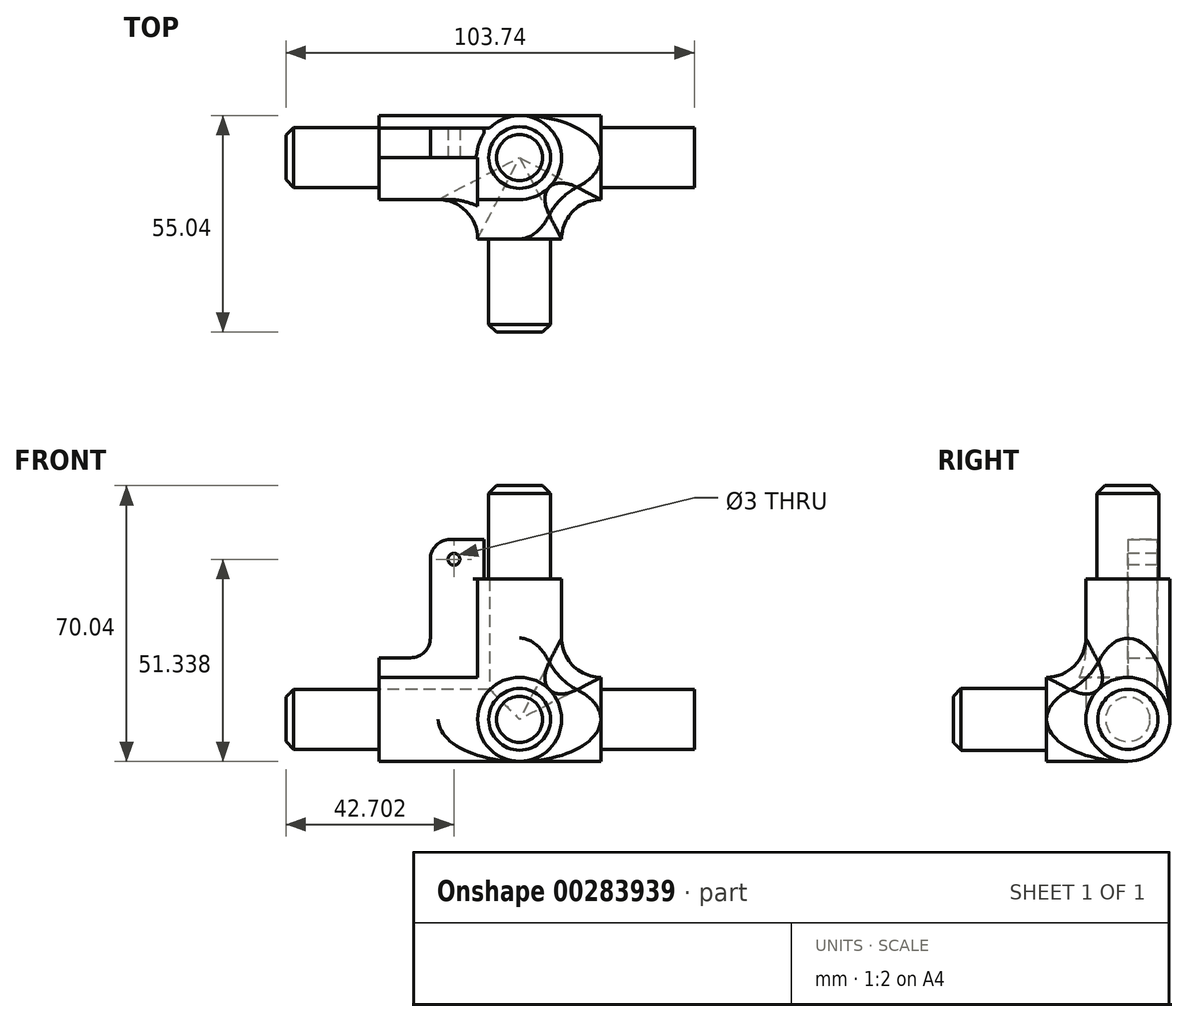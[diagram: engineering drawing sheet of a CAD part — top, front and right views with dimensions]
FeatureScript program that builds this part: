
annotation { "Feature Type Name" : "Feature", "Feature Type Description" : "" }
export const myFeature = defineFeature(function(context is Context, id is Id, definition is map)
    precondition{}
    {
        {
            var Q0;
            Q0=qCreatedBy(makeId("Right.planeOp"),FACE);
            var sketch = newSketch(context, id + "F0", { "sketchPlane" : qUnion([Q0])});
            skCircle(sketch, "E0", {"center": v(0, 0) * mm, "radius": 10.67 * mm});
            skSolve(sketch);
        }
        {
            var Q0;
            Q0=qSketchRegion(id+"F0",true);
            extrude(context, id + "F1", {"entities" : qUnion([Q0]), "endBound" : BoundingType.SYMMETRIC, "depth" : 21.34 * mm + 20 * mm});
        }
        {
            var Q0;
            Q0=makeQuery(id+"F1.opExtrude","CAP_FACE",FACE,{"disambiguationData":[OSD([sQuery(id+"F0.wireOp",EDGE,"E0")])],"isStart":false});
            var sketch = newSketch(context, id + "F2", { "sketchPlane" : qUnion([Q0])});
            skCircle(sketch, "E1", {"center": v(0, 0) * mm, "radius": 7.9 * mm});
            skSolve(sketch);
        }
        {
            var Q0;
            Q0=qSketchRegion(id+"F2",true);
            extrude(context, id + "F3", {"entities" : qUnion([Q0]), "operationType" : NewBodyOperationType.ADD, "depth" : 15.8 * mm * 1.5});
        }
        {
            var Q0;
            Q0=makeQuery(id+"F3.opExtrude","CAP_FACE",FACE,{"disambiguationData":[OSD([sQuery(id+"F2.wireOp",EDGE,"E1")])],"isStart":false});
            var sketch = newSketch(context, id + "F4", { "sketchPlane" : qUnion([Q0])});
            skCircle(sketch, "E2.0", {"center": v(0, 0) * mm, "radius": 7.9 * mm});
            skCircle(sketch, "E3", {"center": v(0, 0) * mm, "radius": 7.65 * mm});
            skSolve(sketch);
        }
        {
            var Q0;
            Q0=qSketchRegion(id+"F4",true);
            var Q1;
            Q1=makeQuery(id+"F1.opExtrude","CAP_FACE",FACE,{"disambiguationData":[OSD([sQuery(id+"F0.wireOp",EDGE,"E0")])],"isStart":false});
            extrude(context, id + "F5", {"entities" : qUnion([Q0]), "operationType" : NewBodyOperationType.REMOVE, "endBound" : BoundingType.UP_TO_SURFACE, "oppositeDirection" : true, "endBoundEntityFace" : qUnion([Q1]), "depth" : 25 * mm});
        }
        {
            var Q0;
            Q0=makeQuery(id+"F1.opExtrude","CAP_FACE",FACE,{"disambiguationData":[OSD([sQuery(id+"F0.wireOp",EDGE,"E0")])],"isStart":true});
            var sketch = newSketch(context, id + "F6", { "sketchPlane" : qUnion([Q0])});
            skCircle(sketch, "E4", {"center": v(0, 0) * mm, "radius": 7.65 * mm});
            skSolve(sketch);
        }
        {
            var Q0;
            Q0=qSketchRegion(id+"F6",true);
            extrude(context, id + "F7", {"entities" : qUnion([Q0]), "operationType" : NewBodyOperationType.ADD, "depth" : 15.8 * mm * 1.5 + 15 * mm});
        }
        {
            var Q0;
            Q0=qCreatedBy(makeId("Top.planeOp"),FACE);
            var sketch = newSketch(context, id + "F8", { "sketchPlane" : qUnion([Q0])});
            skCircle(sketch, "E5", {"center": v(0, 0) * mm, "radius": 10.67 * mm});
            skSolve(sketch);
        }
        {
            var Q0;
            Q0=qSketchRegion(id+"F8",true);
            extrude(context, id + "F9", {"entities" : qUnion([Q0]), "operationType" : NewBodyOperationType.ADD, "depth" : 21.34 * mm / 2 + 25 * mm});
        }
        {
            var Q0;
            Q0=makeQuery(id+"F9.opExtrude","CAP_FACE",FACE,{"disambiguationData":[OSD([sQuery(id+"F8.wireOp",EDGE,"E5")])],"isStart":false});
            var sketch = newSketch(context, id + "F10", { "sketchPlane" : qUnion([Q0])});
            skCircle(sketch, "E6", {"center": v(0, 0) * mm, "radius": 7.84 * mm});
            skSolve(sketch);
        }
        {
            var Q0;
            Q0=qSketchRegion(id+"F10",true);
            extrude(context, id + "F11", {"entities" : qUnion([Q0]), "operationType" : NewBodyOperationType.ADD, "depth" : 15.8 * mm * 1.5});
        }
        {
            var Q0;
            Q0=qCreatedBy(makeId("Front.planeOp"),FACE);
            var sketch = newSketch(context, id + "F12", { "sketchPlane" : qUnion([Q0])});
            skCircle(sketch, "E7", {"center": v(0, 0) * mm, "radius": 10.67 * mm});
            skSolve(sketch);
        }
        {
            var Q0;
            Q0=qSketchRegion(id+"F12",true);
            extrude(context, id + "F13", {"entities" : qUnion([Q0]), "operationType" : NewBodyOperationType.ADD, "depth" : 21.34 * mm / 2 + 10 * mm});
        }
        {
            var Q0;
            Q0=makeQuery(id+"F13.opExtrude","CAP_FACE",FACE,{"disambiguationData":[OSD([sQuery(id+"F12.wireOp",EDGE,"E7")])],"isStart":false});
            var sketch = newSketch(context, id + "F14", { "sketchPlane" : qUnion([Q0])});
            skCircle(sketch, "E8", {"center": v(0, 0) * mm, "radius": 7.84 * mm});
            skSolve(sketch);
        }
        {
            var Q0;
            Q0=qSketchRegion(id+"F14",true);
            extrude(context, id + "F15", {"entities" : qUnion([Q0]), "operationType" : NewBodyOperationType.ADD, "depth" : 15.8 * mm * 1.5});
        }
        {
            var Q0;
            Q0=makeQuery(id+"F11.opExtrude","CAP_EDGE",EDGE,{"disambiguationData":[OSD([sQuery(id+"F10.wireOp",EDGE,"E6")])],"isStart":false});
            var Q1;
            Q1=makeQuery(id+"F5.boolean.opBoolean","COPY",EDGE,{"derivedFrom":makeQuery(id+"F5.opExtrude","CAP_EDGE",EDGE,{"disambiguationData":[OSD([sQuery(id+"F4.wireOp",EDGE,"E3")])],"isStart":true})});
            var Q2;
            Q2=makeQuery(id+"F7.opExtrude","CAP_EDGE",EDGE,{"disambiguationData":[OSD([sQuery(id+"F6.wireOp",EDGE,"E4")])],"isStart":false});
            var Q3;
            Q3=makeQuery(id+"F15.opExtrude","CAP_EDGE",EDGE,{"disambiguationData":[OSD([sQuery(id+"F14.wireOp",EDGE,"E8")])],"isStart":false});
            chamfer(context, id + "F16", {"entities" : qUnion([Q0, Q1, Q2, Q3]), "width" : 2 * mm, "tangentPropagation" : true});
        }
        {
            var Q0;
            Q0=makeQuery(id+"F1.opExtrude","CAP_FACE",FACE,{"disambiguationData":[OSD([sQuery(id+"F0.wireOp",EDGE,"E0")])],"isStart":true});
            extrude(context, id + "F17", {"entities" : qUnion([Q0]), "operationType" : NewBodyOperationType.ADD, "depth" : 15 * mm});
        }
        {
            var Q0;
            Q0=qCreatedBy(makeId("Front.planeOp"),FACE);
            var sketch = newSketch(context, id + "F18", { "sketchPlane" : qUnion([Q0])});
            skLineSegment(sketch, "E9.0", {"start": v(-35.67, 10.67) * mm, "end": v(-35.67, -10.67) * mm, "construction": true});
            skLineSegment(sketch, "E9.1", {"start": v(-10.67, 35.67) * mm, "end": v(10.67, 35.67) * mm, "construction": true});
            skLineSegment(sketch, "E10.bottom", {"start": v(0, 0) * mm, "end": v(-35.67, 0) * mm});
            skLineSegment(sketch, "E10.top", {"start": v(0, 35.67) * mm, "end": v(-35.67, 35.67) * mm});
            skLineSegment(sketch, "E10.left", {"start": v(0, 0) * mm, "end": v(0, 35.67) * mm});
            skLineSegment(sketch, "E10.right", {"start": v(-35.67, 0) * mm, "end": v(-35.67, 35.67) * mm});
            skSolve(sketch);
        }
        {
            var Q0;
            Q0 = qSketchRegion(id + "F18", true);
            extrude(context, id + "F19", {"entities" : qUnion([Q0]), "operationType" : NewBodyOperationType.ADD, "oppositeDirection" : true, "depth" : 7.5 * mm});
        }
        {
            var Q0;
            Q0=makeQuery(id+"F19.opExtrude","SWEPT_EDGE",EDGE,{"disambiguationData":[OSD([sQuery(id+"F18.wireOp",EDGE,"E10.top"),sQuery(id+"F18.wireOp",EDGE,"E10.right")])]});
            fillet(context, id + "F20", {"entities" : qUnion([Q0]), "radius" : 5 * mm, "tangentPropagation" : true, "allowEdgeOverflow" : false});
        }
        {
            var Q0;
            Q0=makeQuery(id+"F19.boolean.opBoolean","MERGE",FACE,{"derivedFrom":[makeQuery(id+"F9.opExtrude","CAP_FACE",FACE,{"disambiguationData":[OSD([sQuery(id+"F8.wireOp",EDGE,"E5")])],"isStart":false}),makeQuery(id+"F19.opExtrude","SWEPT_FACE",FACE,{"disambiguationData":[OSD([sQuery(id+"F18.wireOp",EDGE,"E10.top")])]})]});
            var sketch = newSketch(context, id + "F21", { "sketchPlane" : qUnion([Q0])});
            skArc(sketch, "E11.0", {"start": v(-10.67, 0) * mm, "mid": v(-7.54, -7.54) * mm, "end": v(0, -10.67) * mm});
            skLineSegment(sketch, "E12", {"start": v(-10.67, 0) * mm, "end": v(-10.67, -10.67) * mm});
            skLineSegment(sketch, "E13", {"start": v(-10.67, -10.67) * mm, "end": v(0, -10.67) * mm});
            skLineSegment(sketch, "E14", {"start": v(0, -10.67) * mm, "end": v(0, 0) * mm, "construction": true});
            skPoint(sketch, "E15.orphan", {"position": v(-7.59, 7.5) * mm});
            skSolve(sketch);
        }
        {
            var Q0;
            Q0 = qSketchRegion(id + "F21", true);
            extrude(context, id + "F22", {"entities" : qUnion([Q0]), "operationType" : NewBodyOperationType.ADD, "endBound" : BoundingType.UP_TO_NEXT, "oppositeDirection" : true, "depth" : 25 * mm});
        }
        {
            var Q0;
            Q0=makeQuery(id+"F19.boolean.opBoolean","MERGE",FACE,{"derivedFrom":[makeQuery(id+"F17.opExtrude","CAP_FACE",FACE,{"disambiguationData":[OSD([sQuery(id+"F0.wireOp",EDGE,"E0")])],"isStart":false}),makeQuery(id+"F19.opExtrude","SWEPT_FACE",FACE,{"disambiguationData":[OSD([sQuery(id+"F18.wireOp",EDGE,"E10.right")])]})]});
            var sketch = newSketch(context, id + "F23", { "sketchPlane" : qUnion([Q0])});
            skArc(sketch, "E16.0", {"start": v(0, 10.67) * mm, "mid": v(7.54, 7.54) * mm, "end": v(10.67, 0) * mm});
            skLineSegment(sketch, "E17", {"start": v(0, 10.67) * mm, "end": v(10.67, 10.67) * mm});
            skLineSegment(sketch, "E18", {"start": v(10.67, 10.67) * mm, "end": v(10.67, 0) * mm});
            skLineSegment(sketch, "E19", {"start": v(10.67, 0) * mm, "end": v(0, 0) * mm, "construction": true});
            skPoint(sketch, "E20.orphan", {"position": v(-7.5, 7.59) * mm});
            skSolve(sketch);
        }
        {
            var Q0;
            Q0 = qSketchRegion(id + "F23", true);
            var Q1;
            Q1=makeQuery(id+"F22.opExtrude","SWEPT_FACE",FACE,{"disambiguationData":[OSD([sQuery(id+"F21.wireOp",EDGE,"E12")])]});
            extrude(context, id + "F24", {"entities" : qUnion([Q0]), "operationType" : NewBodyOperationType.ADD, "endBound" : BoundingType.UP_TO_SURFACE, "oppositeDirection" : true, "endBoundEntityFace" : qUnion([Q1]), "depth" : 25 * mm});
        }
        {
            var Q0;
            Q0=makeQuery(id+"F13.boolean.opBoolean","INTERSECT",EDGE,{"disambiguationData":[OD(0.0)],"derivedFrom":[makeQuery(id+"F1.opExtrude","SWEPT_FACE",FACE,{"disambiguationData":[OSD([sQuery(id+"F0.wireOp",EDGE,"E0")])]}),makeQuery(id+"F13.opExtrude","SWEPT_FACE",FACE,{"disambiguationData":[OSD([sQuery(id+"F12.wireOp",EDGE,"E7")])]})]});
            var Q1;
            Q1=makeQuery(id+"F13.boolean.opBoolean","INTERSECT",EDGE,{"disambiguationData":[OD(1.0)],"derivedFrom":[makeQuery(id+"F1.opExtrude","SWEPT_FACE",FACE,{"disambiguationData":[OSD([sQuery(id+"F0.wireOp",EDGE,"E0")])]}),makeQuery(id+"F13.opExtrude","SWEPT_FACE",FACE,{"disambiguationData":[OSD([sQuery(id+"F12.wireOp",EDGE,"E7")])]})]});
            var Q2;
            Q2=makeQuery(id+"F9.boolean.opBoolean","INTERSECT",EDGE,{"disambiguationData":[OD(1.0)],"derivedFrom":[makeQuery(id+"F1.opExtrude","SWEPT_FACE",FACE,{"disambiguationData":[OSD([sQuery(id+"F0.wireOp",EDGE,"E0")])]}),makeQuery(id+"F9.opExtrude","SWEPT_FACE",FACE,{"disambiguationData":[OSD([sQuery(id+"F8.wireOp",EDGE,"E5")])]})]});
            var Q3;
            Q3=makeQuery(id+"F13.boolean.opBoolean","INTERSECT",EDGE,{"derivedFrom":[makeQuery(id+"F9.opExtrude","SWEPT_FACE",FACE,{"disambiguationData":[OSD([sQuery(id+"F8.wireOp",EDGE,"E5")])]}),makeQuery(id+"F13.opExtrude","SWEPT_FACE",FACE,{"disambiguationData":[OSD([sQuery(id+"F12.wireOp",EDGE,"E7")])]})]});
            fillet(context, id + "F25", {"entities" : qUnion([Q0, Q1, Q2, Q3]), "radius" : 10 * mm, "tangentPropagation" : true, "allowEdgeOverflow" : false});
        }
        {
            var Q0;
            Q0=makeQuery(id+"F22.boolean.opBoolean","MERGE",FACE,{"derivedFrom":[makeQuery(id+"F19.boolean.opBoolean","MERGE",FACE,{"derivedFrom":[makeQuery(id+"F9.opExtrude","CAP_FACE",FACE,{"disambiguationData":[OSD([sQuery(id+"F8.wireOp",EDGE,"E5")])],"isStart":false}),makeQuery(id+"F19.opExtrude","SWEPT_FACE",FACE,{"disambiguationData":[OSD([sQuery(id+"F18.wireOp",EDGE,"E10.top")])]})]}),makeQuery(id+"F22.opExtrude","CAP_FACE",FACE,{"disambiguationData":[OSD([sQuery(id+"F21.wireOp",EDGE,"E11.0"),sQuery(id+"F21.wireOp",EDGE,"E12"),sQuery(id+"F21.wireOp",EDGE,"E13")])],"isStart":true})]});
            var sketch = newSketch(context, id + "F26", { "sketchPlane" : qUnion([Q0])});
            skArc(sketch, "E21", {"start": v(-10.67, 0) * mm, "mid": v(-9.87, 4.05) * mm, "end": v(-7.59, 7.5) * mm, "construction": true});
            skLineSegment(sketch, "E22", {"start": v(-10.67, 0) * mm, "end": v(-10.92, 0) * mm, "construction": true});
            skLineSegment(sketch, "E23", {"start": v(-22.67, 0) * mm, "end": v(-22.67, 7.5) * mm});
            skLineSegment(sketch, "E24", {"start": v(-22.67, 7.5) * mm, "end": v(-7.93, 7.5) * mm});
            skArc(sketch, "E25", {"start": v(-7.93, 7.5) * mm, "mid": v(-10.14, 4.04) * mm, "end": v(-10.92, 0) * mm});
            skLineSegment(sketch, "E26", {"start": v(-7.93, 7.5) * mm, "end": v(-7.59, 7.5) * mm, "construction": true});
            skLineSegment(sketch, "E27", {"start": v(-10.92, 0) * mm, "end": v(-22.67, 0) * mm});
            skSolve(sketch);
        }
        {
            var Q0;
            Q0 = qSketchRegion(id + "F26", true);
            extrude(context, id + "F27", {"entities" : qUnion([Q0]), "operationType" : NewBodyOperationType.ADD, "depth" : 10 * mm});
        }
        {
            var Q0;
            Q0=makeQuery(id+"F27.boolean.opBoolean","MERGE",FACE,{"derivedFrom":[makeQuery(id+"F19.opExtrude","CAP_FACE",FACE,{"disambiguationData":[OSD([sQuery(id+"F18.wireOp",EDGE,"E10.bottom"),sQuery(id+"F18.wireOp",EDGE,"E10.top"),sQuery(id+"F18.wireOp",EDGE,"E10.left"),sQuery(id+"F18.wireOp",EDGE,"E10.right")])],"isStart":true}),makeQuery(id+"F27.opExtrude","SWEPT_FACE",FACE,{"disambiguationData":[OSD([sQuery(id+"F26.wireOp",EDGE,"E22")])]})]});
            var sketch = newSketch(context, id + "F28", { "sketchPlane" : qUnion([Q0])});
            skCircle(sketch, "E28", {"center": v(-16.67, 40.67) * mm, "radius": 1.5 * mm});
            skSolve(sketch);
        }
        {
            var Q0;
            Q0 = qSketchRegion(id + "F28", true);
            extrude(context, id + "F29", {"entities" : qUnion([Q0]), "operationType" : NewBodyOperationType.REMOVE, "endBound" : BoundingType.THROUGH_ALL, "oppositeDirection" : true, "depth" : 25 * mm});
        }
        {
            var Q0;
            Q0=makeQuery(id+"F27.opExtrude","CAP_EDGE",EDGE,{"disambiguationData":[OSD([sQuery(id+"F26.wireOp",EDGE,"E23")])],"isStart":true});
            var Q1;
            Q1=makeQuery(id+"F27.opExtrude","CAP_EDGE",EDGE,{"disambiguationData":[OSD([sQuery(id+"F26.wireOp",EDGE,"E23")])],"isStart":false});
            fillet(context, id + "F30", {"entities" : qUnion([Q0, Q1]), "radius" : 5 * mm, "tangentPropagation" : true, "allowEdgeOverflow" : false});
        }
        {
            var Q0;
            Q0=makeQuery(id+"F27.opExtrude","SWEPT_EDGE",EDGE,{"disambiguationData":[OSD([sQuery(id+"F21.wireOp",EDGE,"E12"),sQuery(id+"F26.wireOp",EDGE,"E21"),sQuery(id+"F26.wireOp",EDGE,"E22")])]});
            var Q1;
            Q1=makeQuery(id+"F27.opExtrude","SWEPT_EDGE",EDGE,{"disambiguationData":[OSD([sQuery(id+"F8.wireOp",EDGE,"E5"),sQuery(id+"F26.wireOp",EDGE,"E21"),sQuery(id+"F26.wireOp",EDGE,"E24")])]});
            var Q2;
            Q2=makeQuery(id+"F27.opExtrude","SWEPT_EDGE",EDGE,{"disambiguationData":[OSD([sQuery(id+"F18.wireOp",EDGE,"E10.top"),sQuery(id+"F26.wireOp",EDGE,"E25"),sQuery(id+"F26.wireOp",EDGE,"E27")])]});
            fillet(context, id + "F31", {"entities" : qUnion([Q0, Q1, Q2]), "radius" : 1 * mm, "tangentPropagation" : true, "allowEdgeOverflow" : false});
        }
        {
            var Q0;
            Q0=makeQuery(id+"F27.boolean.opBoolean","MERGE",FACE,{"derivedFrom":[makeQuery(id+"F19.opExtrude","CAP_FACE",FACE,{"disambiguationData":[OSD([sQuery(id+"F18.wireOp",EDGE,"E10.bottom"),sQuery(id+"F18.wireOp",EDGE,"E10.top"),sQuery(id+"F18.wireOp",EDGE,"E10.left"),sQuery(id+"F18.wireOp",EDGE,"E10.right")])],"isStart":false}),makeQuery(id+"F27.opExtrude","SWEPT_FACE",FACE,{"disambiguationData":[OSD([sQuery(id+"F26.wireOp",EDGE,"E24")])]})]});
            var sketch = newSketch(context, id + "F32", { "sketchPlane" : qUnion([Q0])});
            skArc(sketch, "E29.0", {"start": v(35.67, 30.67) * mm, "mid": v(34.2, 34.2) * mm, "end": v(30.67, 35.67) * mm});
            skArc(sketch, "E29.1", {"start": v(27.67, 35.67) * mm, "mid": v(24.13, 37.13) * mm, "end": v(22.67, 40.67) * mm});
            skLineSegment(sketch, "E29.2", {"start": v(27.67, 35.67) * mm, "end": v(30.67, 35.67) * mm});
            skLineSegment(sketch, "E30", {"start": v(35.67, 30.67) * mm, "end": v(35.67, 15.67) * mm});
            skLineSegment(sketch, "E31", {"start": v(35.67, 15.67) * mm, "end": v(22.67, 15.67) * mm});
            skLineSegment(sketch, "E32", {"start": v(22.67, 15.67) * mm, "end": v(22.67, 40.67) * mm});
            skSolve(sketch);
        }
        {
            var Q0;
            Q0 = qSketchRegion(id + "F32", true);
            extrude(context, id + "F33", {"entities" : qUnion([Q0]), "operationType" : NewBodyOperationType.REMOVE, "endBound" : BoundingType.UP_TO_NEXT, "oppositeDirection" : true, "depth" : 25 * mm});
        }
        {
            var Q0;
            Q0=makeQuery(id+"F33.boolean.opBoolean","COPY",EDGE,{"derivedFrom":makeQuery(id+"F33.opExtrude","SWEPT_EDGE",EDGE,{"disambiguationData":[OSD([sQuery(id+"F18.wireOp",EDGE,"E10.right"),sQuery(id+"F32.wireOp",EDGE,"E30"),sQuery(id+"F32.wireOp",EDGE,"E31")])]})});
            var Q1;
            Q1=makeQuery(id+"F33.boolean.opBoolean","COPY",EDGE,{"derivedFrom":makeQuery(id+"F33.opExtrude","SWEPT_EDGE",EDGE,{"disambiguationData":[OSD([sQuery(id+"F32.wireOp",EDGE,"E31"),sQuery(id+"F32.wireOp",EDGE,"E32")])]})});
            fillet(context, id + "F34", {"entities" : qUnion([Q0, Q1]), "radius" : 5 * mm, "tangentPropagation" : true, "allowEdgeOverflow" : false});
        }
    });
